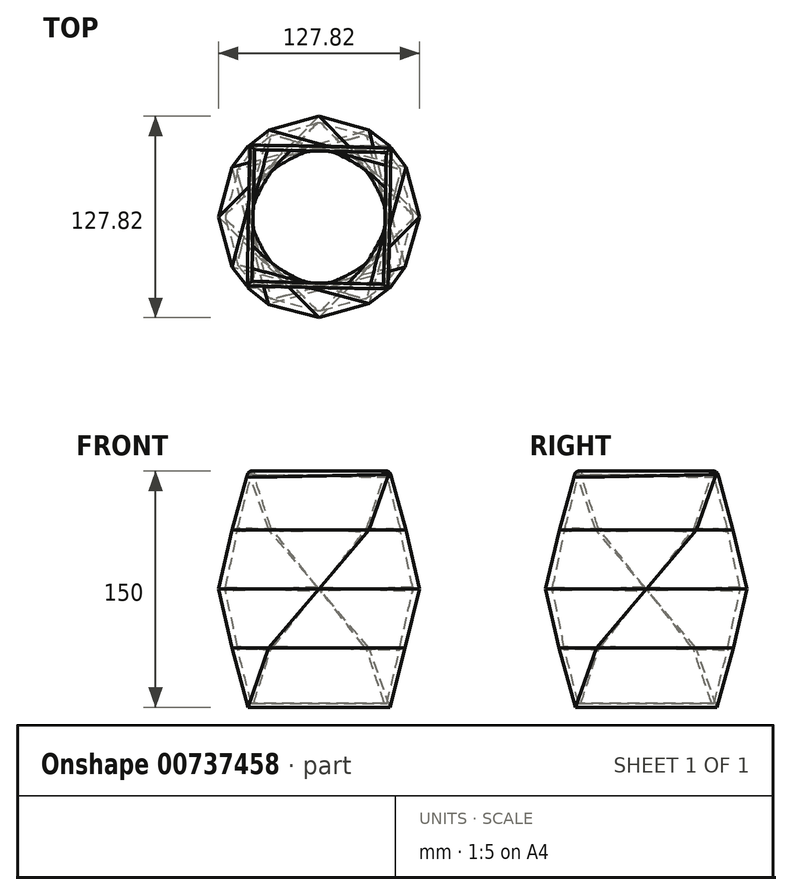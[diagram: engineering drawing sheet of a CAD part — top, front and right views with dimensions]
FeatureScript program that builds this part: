
annotation { "Feature Type Name" : "Feature", "Feature Type Description" : "" }
export const myFeature = defineFeature(function(context is Context, id is Id, definition is map)
    precondition{}
    {
        {
            var Q0;
            Q0=qCreatedBy(makeId("Top.planeOp"),FACE);
            var sketch = newSketch(context, id + "F0", { "sketchPlane" : qUnion([Q0])});
            skLineSegment(sketch, "E0.bottom", {"start": v(45, 45) * mm, "end": v(-45, 45) * mm});
            skLineSegment(sketch, "E0.top", {"start": v(45, -45) * mm, "end": v(-45, -45) * mm});
            skLineSegment(sketch, "E0.left", {"start": v(45, 45) * mm, "end": v(45, -45) * mm});
            skLineSegment(sketch, "E0.right", {"start": v(-45, 45) * mm, "end": v(-45, -45) * mm});
            skPoint(sketch, "E0.middle", {"position": v(0, 0) * mm});
            skSolve(sketch);
        }
        {
            var Q0;
            Q0=qCreatedBy(makeId("Top.planeOp"),FACE);
            cPlane(context, id + "F1", {"entities" : qUnion([Q0]), "cplaneType" : CPlaneType.OFFSET, "offset" : 75 * mm, "width" : 150 * mm, "height" : 150 * mm});
        }
        {
            var Q0;
            Q0=qCreatedBy(id+"F1.planeOp",FACE);
            var sketch = newSketch(context, id + "F2", { "sketchPlane" : qUnion([Q0])});
            skLineSegment(sketch, "E1", {"start": v(0, 63.9) * mm, "end": v(-63.9, 0) * mm});
            skLineSegment(sketch, "E2", {"start": v(-63.9, 0) * mm, "end": v(0, -63.9) * mm});
            skLineSegment(sketch, "E3", {"start": v(0, -63.9) * mm, "end": v(63.9, 0) * mm});
            skLineSegment(sketch, "E4", {"start": v(63.9, 0) * mm, "end": v(0, 63.9) * mm});
            skSolve(sketch);
        }
        {
            var Q0;
            Q0=qCreatedBy(id+"F1.planeOp",FACE);
            cPlane(context, id + "F3", {"entities" : qUnion([Q0]), "cplaneType" : CPlaneType.OFFSET, "offset" : 75 * mm, "width" : 150 * mm, "height" : 150 * mm});
        }
        {
            var Q0;
            Q0=qCreatedBy(id+"F3.planeOp",FACE);
            var sketch = newSketch(context, id + "F4", { "sketchPlane" : qUnion([Q0])});
            skLineSegment(sketch, "E5.bottom", {"start": v(45, 45) * mm, "end": v(-45, 45) * mm});
            skLineSegment(sketch, "E5.top", {"start": v(45, -45) * mm, "end": v(-45, -45) * mm});
            skLineSegment(sketch, "E5.left", {"start": v(45, 45) * mm, "end": v(45, -45) * mm});
            skLineSegment(sketch, "E5.right", {"start": v(-45, 45) * mm, "end": v(-45, -45) * mm});
            skPoint(sketch, "E5.middle", {"position": v(0, 0) * mm});
            skSolve(sketch);
        }
        {
            var Q0;
            Q0=makeQuery(id+"F0.imprint","IMPRINT",FACE,{"disambiguationData":[TD([[makeQuery(id+"F0.imprint","IMPRINT",EDGE,{"derivedFrom":sQuery(id+"F0.wireOp",EDGE,"E0.bottom")}),1.0]])]});
            cPlane(context, id + "F5", {"entities" : qUnion([Q0]), "cplaneType" : CPlaneType.OFFSET, "offset" : 37.5 * mm, "width" : 150 * mm, "height" : 150 * mm});
        }
        {
            var Q0;
            Q0=qCreatedBy(id+"F5.planeOp",FACE);
            var sketch = newSketch(context, id + "F6", { "sketchPlane" : qUnion([Q0])});
            skLineSegment(sketch, "E6", {"start": v(-32.22, -55.48) * mm, "end": v(-55.15, 31.55) * mm});
            skLineSegment(sketch, "E7", {"start": v(-55.15, 31.55) * mm, "end": v(31.69, 55.2) * mm});
            skLineSegment(sketch, "E8", {"start": v(31.69, 55.2) * mm, "end": v(54.62, -31.83) * mm});
            skLineSegment(sketch, "E9", {"start": v(54.62, -31.83) * mm, "end": v(-32.22, -55.48) * mm});
            skSolve(sketch);
        }
        {
            var Q0;
            Q0=qCreatedBy(makeId("Top.planeOp"),FACE);
            cPlane(context, id + "F7", {"entities" : qUnion([Q0]), "cplaneType" : CPlaneType.OFFSET, "offset" : 112.5 * mm, "width" : 150 * mm, "height" : 150 * mm});
        }
        {
            var Q0;
            Q0=qCreatedBy(id+"F7.planeOp",FACE);
            var sketch = newSketch(context, id + "F8", { "sketchPlane" : qUnion([Q0])});
            skLineSegment(sketch, "E10", {"start": v(-55.25, -31.9) * mm, "end": v(-31.89, 55.02) * mm});
            skLineSegment(sketch, "E11", {"start": v(-31.89, 55.02) * mm, "end": v(55.07, 31.8) * mm});
            skLineSegment(sketch, "E12", {"start": v(55.07, 31.8) * mm, "end": v(31.7, -55.12) * mm});
            skLineSegment(sketch, "E13", {"start": v(31.7, -55.12) * mm, "end": v(-55.25, -31.9) * mm});
            skSolve(sketch);
        }
        {
            var Q0;
            Q0=makeQuery(id+"F0.imprint","IMPRINT",FACE,{"disambiguationData":[TD([[makeQuery(id+"F0.imprint","IMPRINT",EDGE,{"derivedFrom":sQuery(id+"F0.wireOp",EDGE,"E0.bottom")}),1.0]])]});
            var Q1;
            Q1=makeQuery(id+"F6.imprint","IMPRINT",FACE,{"disambiguationData":[TD([[makeQuery(id+"F6.imprint","IMPRINT",EDGE,{"derivedFrom":sQuery(id+"F6.wireOp",EDGE,"E6")}),-1.0]])]});
            loft(context, id + "F9", {"sheetProfilesArray" : [{ "sheetProfileEntities" : qUnion([Q0]) }, { "sheetProfileEntities" : qUnion([Q1]) }]});
        }
        {
            var Q1;
            Q1=makeQuery(id+"F9.opLoft","CAP_FACE",FACE,{"disambiguationData":[OSD([makeQuery(id+"F6.imprint","IMPRINT",FACE,{"disambiguationData":[TD([[makeQuery(id+"F6.imprint","IMPRINT",EDGE,{"derivedFrom":sQuery(id+"F6.wireOp",EDGE,"E6")}),-1.0]])]})])],"isStart":true});
            var Q2;
            Q2=makeQuery(id+"F2.imprint","IMPRINT",FACE,{"disambiguationData":[TD([[makeQuery(id+"F2.imprint","IMPRINT",EDGE,{"derivedFrom":sQuery(id+"F2.wireOp",EDGE,"E1")}),1.0]])]});
            loft(context, id + "F10", {"operationType" : NewBodyOperationType.ADD, "sheetProfilesArray" : [{ "sheetProfileEntities" : qUnion([Q1]) }, { "sheetProfileEntities" : qUnion([Q2]) }]});
        }
        {
            var Q1;
            Q1=makeQuery(id+"F2.imprint","IMPRINT",FACE,{"disambiguationData":[TD([[makeQuery(id+"F2.imprint","IMPRINT",EDGE,{"derivedFrom":sQuery(id+"F2.wireOp",EDGE,"E1")}),1.0]])]});
            var Q2;
            Q2=makeQuery(id+"F8.imprint","IMPRINT",FACE,{"disambiguationData":[TD([[makeQuery(id+"F8.imprint","IMPRINT",EDGE,{"derivedFrom":sQuery(id+"F8.wireOp",EDGE,"E10")}),-1.0]])]});
            loft(context, id + "F11", {"operationType" : NewBodyOperationType.ADD, "sheetProfilesArray" : [{ "sheetProfileEntities" : qUnion([Q1]) }, { "sheetProfileEntities" : qUnion([Q2]) }]});
        }
        {
            var Q1;
            Q1=makeQuery(id+"F11.opLoft","CAP_FACE",FACE,{"disambiguationData":[OSD([makeQuery(id+"F8.imprint","IMPRINT",FACE,{"disambiguationData":[TD([[makeQuery(id+"F8.imprint","IMPRINT",EDGE,{"derivedFrom":sQuery(id+"F8.wireOp",EDGE,"E10")}),-1.0]])]})])],"isStart":true});
            var Q2;
            Q2=makeQuery(id+"F4.imprint","IMPRINT",FACE,{"disambiguationData":[TD([[makeQuery(id+"F4.imprint","IMPRINT",EDGE,{"derivedFrom":sQuery(id+"F4.wireOp",EDGE,"E5.bottom")}),1.0]])]});
            loft(context, id + "F12", {"operationType" : NewBodyOperationType.ADD, "sheetProfilesArray" : [{ "sheetProfileEntities" : qUnion([Q1]) }, { "sheetProfileEntities" : qUnion([Q2]) }]});
        }
        {
            var Q0;
            Q0=makeQuery(id+"F12.opLoft","MID_CAP_EDGE",EDGE,{"disambiguationData":[OSD([sQuery(id+"F4.wireOp",EDGE,"E5.top"),sQuery(id+"F4.wireOp",EDGE,"E5.left"),sQuery(id+"F4.wireOp",EDGE,"E5.right")])],"capPos":1.0});
            var Q1;
            Q1=makeQuery(id+"F12.opLoft","MID_CAP_EDGE",EDGE,{"disambiguationData":[OSD([sQuery(id+"F4.wireOp",EDGE,"E5.bottom"),sQuery(id+"F4.wireOp",EDGE,"E5.top"),sQuery(id+"F4.wireOp",EDGE,"E5.left")])],"capPos":1.0});
            var Q2;
            Q2=makeQuery(id+"F12.opLoft","MID_CAP_EDGE",EDGE,{"disambiguationData":[OSD([sQuery(id+"F4.wireOp",EDGE,"E5.bottom"),sQuery(id+"F4.wireOp",EDGE,"E5.left"),sQuery(id+"F4.wireOp",EDGE,"E5.right")])],"capPos":1.0});
            var Q3;
            Q3=makeQuery(id+"F12.opLoft","MID_CAP_EDGE",EDGE,{"disambiguationData":[OSD([sQuery(id+"F4.wireOp",EDGE,"E5.bottom"),sQuery(id+"F4.wireOp",EDGE,"E5.top"),sQuery(id+"F4.wireOp",EDGE,"E5.right")])],"capPos":1.0});
            fillet(context, id + "F13", {"entities" : qUnion([Q0, Q1, Q2, Q3]), "radius" : 3 * mm, "tangentPropagation" : true, "allowEdgeOverflow" : false});
        }
        {
            var Q0;
            Q0=makeQuery(id+"F12.opLoft","CAP_FACE",FACE,{"disambiguationData":[OSD([makeQuery(id+"F4.imprint","IMPRINT",FACE,{"disambiguationData":[TD([[makeQuery(id+"F4.imprint","IMPRINT",EDGE,{"derivedFrom":sQuery(id+"F4.wireOp",EDGE,"E5.bottom")}),1.0]])]})])],"isStart":true});
            shell(context, id + "F14", {"entities" : qUnion([Q0]), "thickness" : 2.5 * mm});
        }
    });
